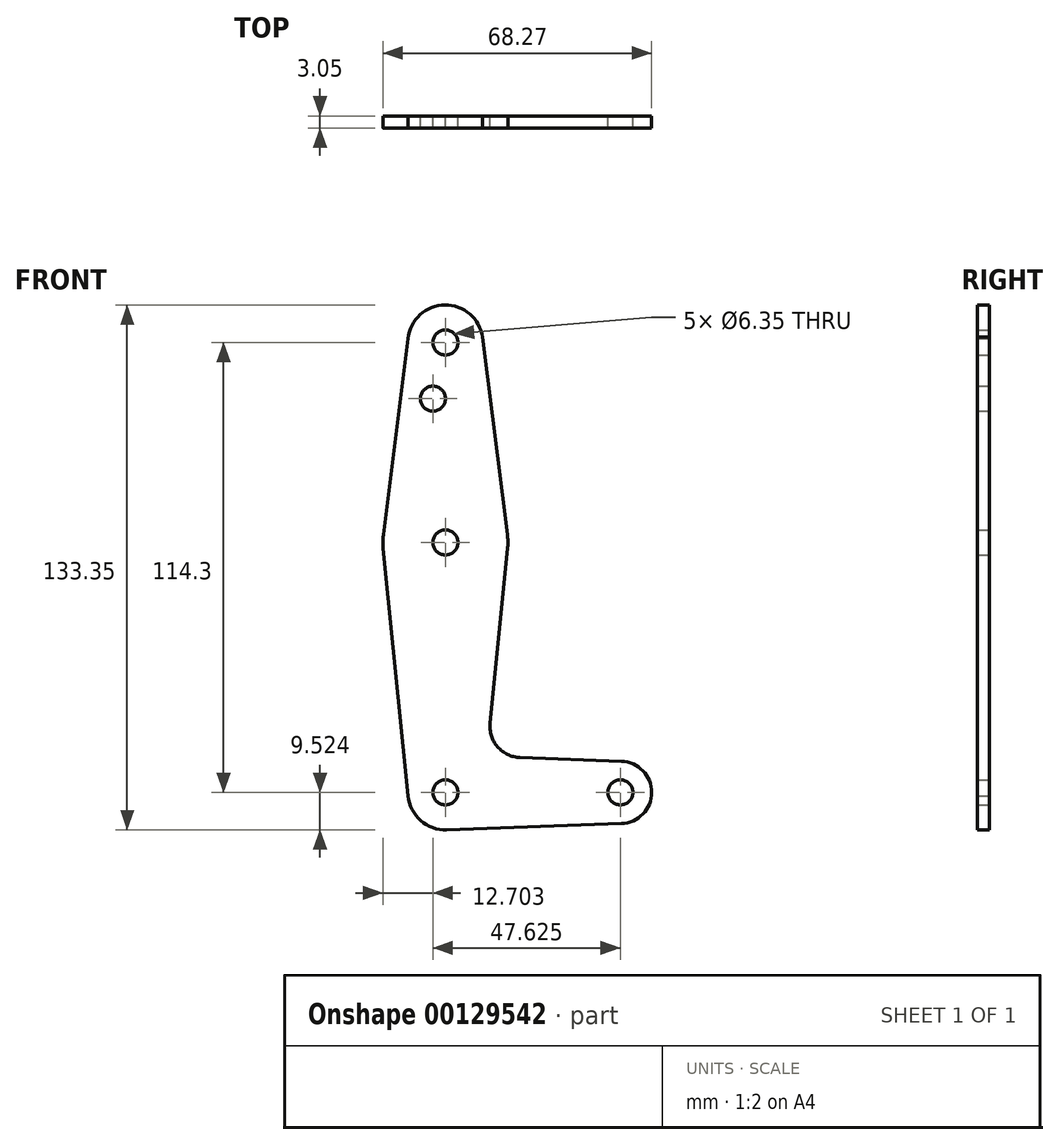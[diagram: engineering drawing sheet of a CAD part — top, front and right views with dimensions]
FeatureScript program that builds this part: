
annotation { "Feature Type Name" : "Feature", "Feature Type Description" : "" }
export const myFeature = defineFeature(function(context is Context, id is Id, definition is map)
    precondition{}
    {
        {
            var Q0;
            Q0=qCreatedBy(makeId("Front.planeOp"),FACE);
            var sketch = newSketch(context, id + "F0", { "sketchPlane" : qUnion([Q0])});
            skLineSegment(sketch, "E0", {"start": v(-33.18, 95.76) * mm, "end": v(-33.18, -18.54) * mm, "construction": true});
            skLineSegment(sketch, "E1", {"start": v(-33.18, -18.54) * mm, "end": v(11.27, -18.54) * mm, "construction": true});
            skCircle(sketch, "E2", {"center": v(-33.18, 95.76) * mm, "radius": 9.53 * mm});
            skCircle(sketch, "E3", {"center": v(-33.18, 44.96) * mm, "radius": 15.88 * mm});
            skCircle(sketch, "E4", {"center": v(-33.18, -18.54) * mm, "radius": 9.53 * mm});
            skCircle(sketch, "E5", {"center": v(11.27, -18.54) * mm, "radius": 7.94 * mm});
            skLineSegment(sketch, "E6", {"start": v(-14.22, -9.68) * mm, "end": v(11.55, -10.6) * mm});
            skLineSegment(sketch, "E7", {"start": v(-32.84, -28.05) * mm, "end": v(11.55, -26.47) * mm});
            skLineSegment(sketch, "E8", {"start": v(-48.98, 43.38) * mm, "end": v(-42.67, -19.37) * mm});
            skLineSegment(sketch, "E9", {"start": v(-17.39, 43.38) * mm, "end": v(-21.84, -0.94) * mm});
            skLineSegment(sketch, "E10", {"start": v(-42.65, 96.8) * mm, "end": v(-48.93, 46.95) * mm});
            skLineSegment(sketch, "E11", {"start": v(-23.75, 97.1) * mm, "end": v(-17.43, 46.95) * mm});
            skCircle(sketch, "E12", {"center": v(-33.18, 95.76) * mm, "radius": 3.18 * mm});
            skCircle(sketch, "E13", {"center": v(-33.18, 44.96) * mm, "radius": 3.18 * mm});
            skCircle(sketch, "E14", {"center": v(-33.18, -18.54) * mm, "radius": 3.18 * mm});
            skCircle(sketch, "E15", {"center": v(11.27, -18.54) * mm, "radius": 3.18 * mm});
            skCircle(sketch, "E16", {"center": v(-36.36, 81.49) * mm, "radius": 3.18 * mm});
            skArc(sketch, "E17.filletArc", {"start": v(-21.84, -0.94) * mm, "mid": v(-19.92, -6.96) * mm, "end": v(-14.22, -9.68) * mm});
            skSolve(sketch);
        }
        {
            var Q0;
            Q0=makeQuery(id+"F0.imprint","IMPRINT",FACE,{"disambiguationData":[TD([[makeQuery(id+"F0.imprint","IMPRINT",EDGE,{"derivedFrom":sQuery(id+"F0.wireOp",EDGE,"E12")}),-1.0]])]});
            var Q1;
            {var subQ0=sQuery(id+"F0.wireOp",EDGE,"E10");Q1=makeQuery(id+"F0.imprint","IMPRINT",FACE,{"disambiguationData":[TD([[makeQuery(id+"F0.imprint","IMPRINT",EDGE,{"derivedFrom":subQ0}),1.0]])]});}
            var Q2;
            Q2=makeQuery(id+"F0.imprint","IMPRINT",FACE,{"disambiguationData":[TD([[makeQuery(id+"F0.imprint","IMPRINT",EDGE,{"derivedFrom":sQuery(id+"F0.wireOp",EDGE,"E13")}),-1.0]])]});
            var Q3;
            {var subQ0=sQuery(id+"F0.wireOp",EDGE,"E6");Q3=makeQuery(id+"F0.imprint","IMPRINT",FACE,{"disambiguationData":[TD([[makeQuery(id+"F0.imprint","IMPRINT",EDGE,{"derivedFrom":subQ0}),-1.0]])]});}
            var Q4;
            Q4=makeQuery(id+"F0.imprint","IMPRINT",FACE,{"disambiguationData":[TD([[makeQuery(id+"F0.imprint","IMPRINT",EDGE,{"derivedFrom":sQuery(id+"F0.wireOp",EDGE,"E14")}),-1.0]])]});
            var Q5;
            Q5=makeQuery(id+"F0.imprint","IMPRINT",FACE,{"disambiguationData":[TD([[makeQuery(id+"F0.imprint","IMPRINT",EDGE,{"derivedFrom":sQuery(id+"F0.wireOp",EDGE,"E15")}),-1.0]])]});
            extrude(context, id + "F1", {"entities" : qUnion([Q0, Q1, Q2, Q3, Q4, Q5]), "depth" : 3.05 * mm});
        }
    });
